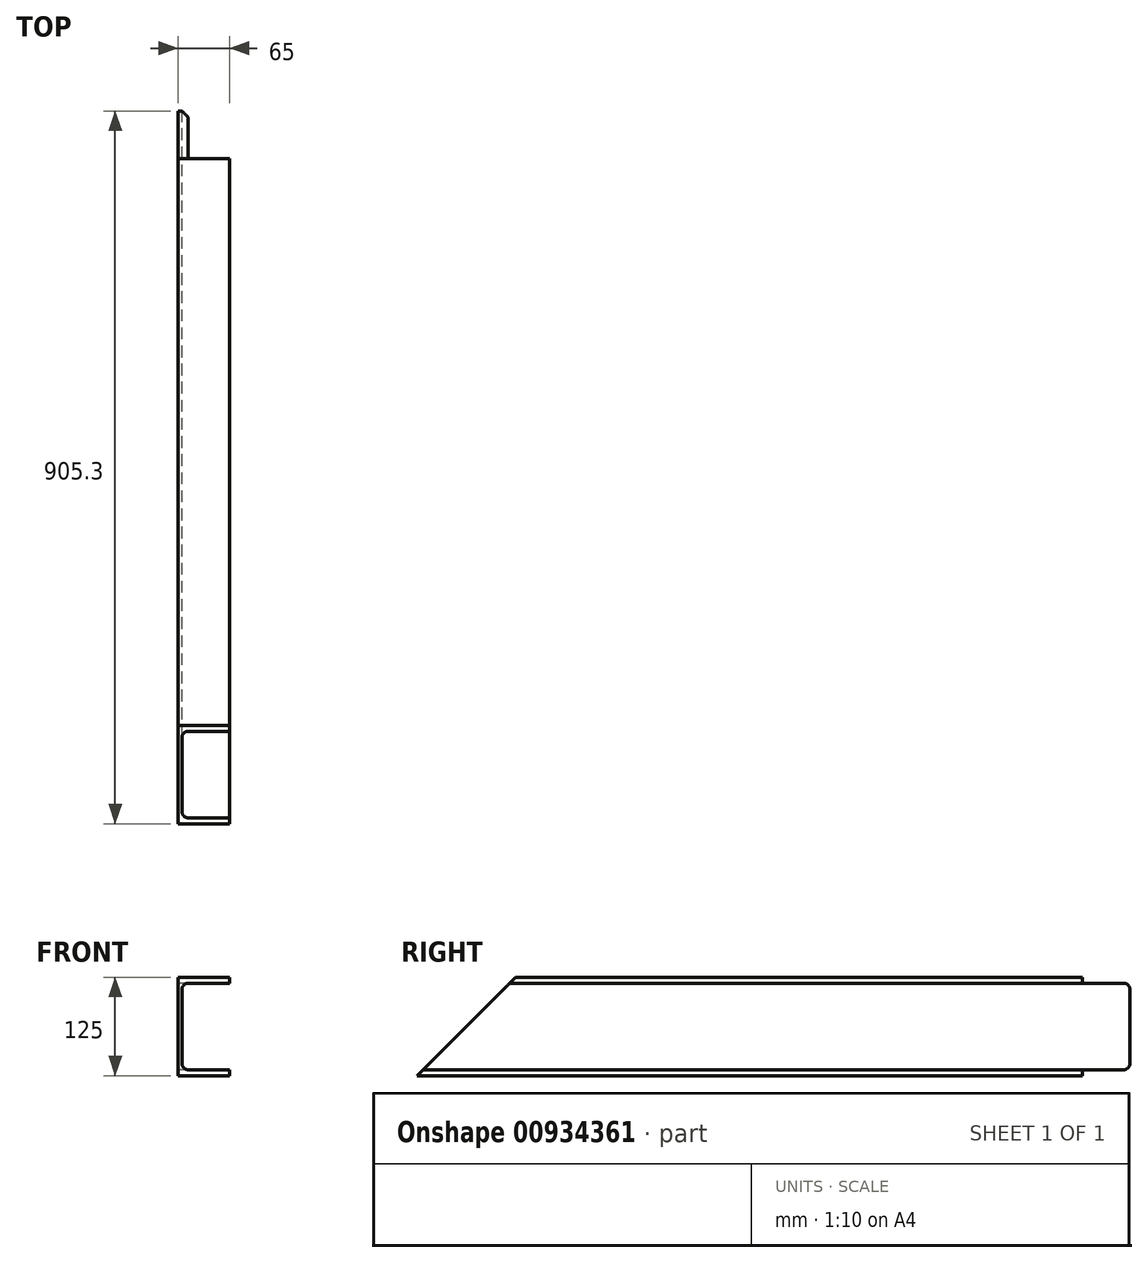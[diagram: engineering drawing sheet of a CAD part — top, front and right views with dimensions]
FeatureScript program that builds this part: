
annotation { "Feature Type Name" : "Feature", "Feature Type Description" : "" }
export const myFeature = defineFeature(function(context is Context, id is Id, definition is map)
    precondition{}
    {
        {
            var Q0;
            Q0=qCreatedBy(makeId("Front.planeOp"),FACE);
            var sketch = newSketch(context, id + "F0", { "sketchPlane" : qUnion([Q0])});
            skLineSegment(sketch, "E0", {"start": v(-25.17, -62.5) * mm, "end": v(-25.17, 62.5) * mm});
            skLineSegment(sketch, "E1", {"start": v(-25.17, 62.5) * mm, "end": v(39.83, 62.5) * mm});
            skLineSegment(sketch, "E2", {"start": v(39.83, 62.5) * mm, "end": v(39.83, 55) * mm});
            skLineSegment(sketch, "E3", {"start": v(39.83, 55) * mm, "end": v(-12.47, 55) * mm});
            skLineSegment(sketch, "E4", {"start": v(-25.17, -62.5) * mm, "end": v(39.83, -62.5) * mm});
            skLineSegment(sketch, "E5", {"start": v(39.83, -62.5) * mm, "end": v(39.83, -55) * mm});
            skLineSegment(sketch, "E6", {"start": v(39.83, -55) * mm, "end": v(-12.47, -55) * mm});
            skLineSegment(sketch, "E7", {"start": v(-20.47, -47) * mm, "end": v(-20.47, 47) * mm});
            skPoint(sketch, "E8.visualSharp", {"position": v(-20.47, 55) * mm});
            skArc(sketch, "E8.filletArc", {"start": v(-12.47, 55) * mm, "mid": v(-18.12, 52.66) * mm, "end": v(-20.47, 47) * mm});
            skPoint(sketch, "E9.visualSharp", {"position": v(-20.47, -55) * mm});
            skArc(sketch, "E9.filletArc", {"start": v(-20.47, -47) * mm, "mid": v(-18.12, -52.66) * mm, "end": v(-12.47, -55) * mm});
            skSolve(sketch);
        }
        {
            var Q0;
            Q0=makeQuery(id+"F0.imprint","IMPRINT",FACE,{"disambiguationData":[TD([[makeQuery(id+"F0.imprint","IMPRINT",EDGE,{"derivedFrom":sQuery(id+"F0.wireOp",EDGE,"E0")}),-1.0]])]});
            extrude(context, id + "F1", {"entities" : qUnion([Q0]), "depth" : 910 * mm, "offsetDistance" : 25 * mm});
        }
        {
            var Q0;
            Q0=makeQuery(id+"F1.opExtrude","SWEPT_FACE",FACE,{"disambiguationData":[OSD([sQuery(id+"F0.wireOp",EDGE,"E0")])]});
            var sketch = newSketch(context, id + "F2", { "sketchPlane" : qUnion([Q0])});
            skLineSegment(sketch, "E10", {"start": v(0, -62.5) * mm, "end": v(0, 62.5) * mm});
            skLineSegment(sketch, "E11", {"start": v(0, 62.5) * mm, "end": v(65, 62.5) * mm});
            skLineSegment(sketch, "E12", {"start": v(65, 62.5) * mm, "end": v(65, 55) * mm});
            skLineSegment(sketch, "E13", {"start": v(65, 55) * mm, "end": v(12.7, 55) * mm});
            skLineSegment(sketch, "E14", {"start": v(0, -62.5) * mm, "end": v(65, -62.5) * mm});
            skLineSegment(sketch, "E15", {"start": v(65, -62.5) * mm, "end": v(65, -55) * mm});
            skLineSegment(sketch, "E16", {"start": v(65, -55) * mm, "end": v(12.7, -55) * mm});
            skLineSegment(sketch, "E17", {"start": v(4.7, -47) * mm, "end": v(4.7, 47) * mm});
            skPoint(sketch, "E18.visualSharp", {"position": v(4.7, 55) * mm});
            skArc(sketch, "E18.filletArc", {"start": v(12.7, 55) * mm, "mid": v(7.04, 52.66) * mm, "end": v(4.7, 47) * mm});
            skPoint(sketch, "E19.visualSharp", {"position": v(4.7, -55) * mm});
            skArc(sketch, "E19.filletArc", {"start": v(4.7, -47) * mm, "mid": v(7.04, -52.66) * mm, "end": v(12.7, -55) * mm});
            skLineSegment(sketch, "E20", {"start": v(910, 62.5) * mm, "end": v(785, 62.5) * mm});
            skLineSegment(sketch, "E21", {"start": v(785, 62.5) * mm, "end": v(910, -62.5) * mm});
            skSolve(sketch);
        }
        {
            var Q0;
            Q0=makeQuery(id+"F2.imprint","IMPRINT",FACE,{"disambiguationData":[TD([[makeQuery(id+"F2.imprint","IMPRINT",EDGE,{"derivedFrom":sQuery(id+"F2.wireOp",EDGE,"E10")}),-1.0]])]});
            var Q1;
            Q1=makeQuery(id+"F2.imprint","IMPRINT",FACE,{"disambiguationData":[TD([[makeQuery(id+"F2.imprint","IMPRINT",EDGE,{"derivedFrom":sQuery(id+"F2.wireOp",EDGE,"E20")}),1.0]])]});
            extrude(context, id + "F3", {"entities" : qUnion([Q0, Q1]), "operationType" : NewBodyOperationType.REMOVE, "endBound" : BoundingType.THROUGH_ALL, "oppositeDirection" : true, "depth" : 25 * mm, "offsetDistance" : 25 * mm});
        }
    });
